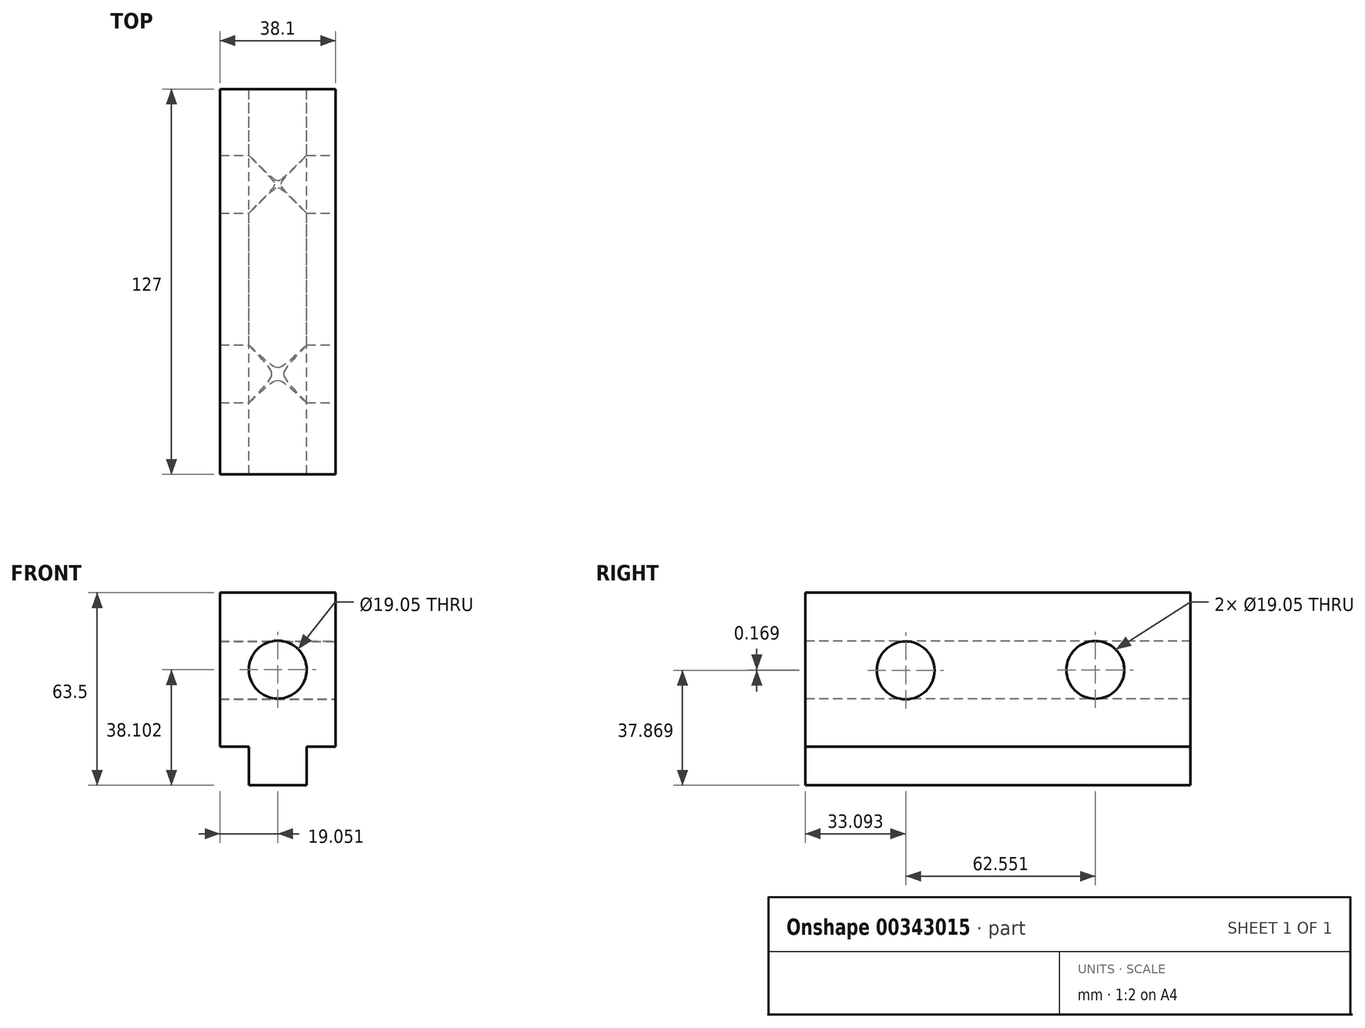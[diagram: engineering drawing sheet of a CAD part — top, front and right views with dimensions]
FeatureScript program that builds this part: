
annotation { "Feature Type Name" : "Feature", "Feature Type Description" : "" }
export const myFeature = defineFeature(function(context is Context, id is Id, definition is map)
    precondition{}
    {
        {
            var Q0;
            Q0=qCreatedBy(makeId("Front.planeOp"),FACE);
            var sketch = newSketch(context, id + "F0", { "sketchPlane" : qUnion([Q0])});
            skLineSegment(sketch, "E0", {"start": v(9.05, -26.38) * mm, "end": v(-10, -26.38) * mm});
            skLineSegment(sketch, "E1", {"start": v(-10, -26.38) * mm, "end": v(-10, -13.68) * mm});
            skLineSegment(sketch, "E2", {"start": v(9.05, -26.38) * mm, "end": v(9.05, -13.68) * mm});
            skLineSegment(sketch, "E3", {"start": v(-10, -13.68) * mm, "end": v(-19.53, -13.68) * mm});
            skLineSegment(sketch, "E4", {"start": v(9.05, -13.68) * mm, "end": v(18.57, -13.68) * mm});
            skLineSegment(sketch, "E5", {"start": v(-19.53, -13.68) * mm, "end": v(-19.53, 37.12) * mm});
            skLineSegment(sketch, "E6", {"start": v(18.57, -13.68) * mm, "end": v(18.57, 37.12) * mm});
            skLineSegment(sketch, "E7", {"start": v(-19.53, 37.12) * mm, "end": v(18.57, 37.12) * mm});
            skCircle(sketch, "E8", {"center": v(-0.48, 11.72) * mm, "radius": 9.53 * mm});
            skSolve(sketch);
        }
        {
            var Q0;
            Q0 = qSketchRegion(id + "F0", true);
            extrude(context, id + "F1", {"entities" : qUnion([Q0]), "depth" : 127 * mm});
        }
        {
            var Q0;
            Q0=qCreatedBy(makeId("Right.planeOp"),FACE);
            var sketch = newSketch(context, id + "F2", { "sketchPlane" : qUnion([Q0])});
            skLineSegment(sketch, "E9", {"start": v(-124.68, -13.43) * mm, "end": v(0, -13.43) * mm});
            skCircle(sketch, "E10", {"center": v(-93.9, 11.49) * mm, "radius": 9.53 * mm});
            skCircle(sketch, "E11", {"center": v(-31.36, 11.66) * mm, "radius": 9.53 * mm});
            skPoint(sketch, "E12.start.orphan", {"position": v(-62.71, 36.74) * mm});
            skPoint(sketch, "E13.orphan", {"position": v(-62.71, -13.43) * mm});
            skPoint(sketch, "E14.orphan", {"position": v(0, 36.74) * mm});
            skSolve(sketch);
        }
        {
            var Q0;
            Q0 = qSketchRegion(id + "F2", true);
            extrude(context, id + "F3", {"entities" : qUnion([Q0]), "operationType" : NewBodyOperationType.REMOVE, "oppositeDirection" : true, "depth" : 34.8 * mm});
        }
        {
            var Q0;
            Q0 = qSketchRegion(id + "F2", true);
            extrude(context, id + "F4", {"entities" : qUnion([Q0]), "operationType" : NewBodyOperationType.REMOVE, "depth" : 22.86 * mm});
        }
    });
